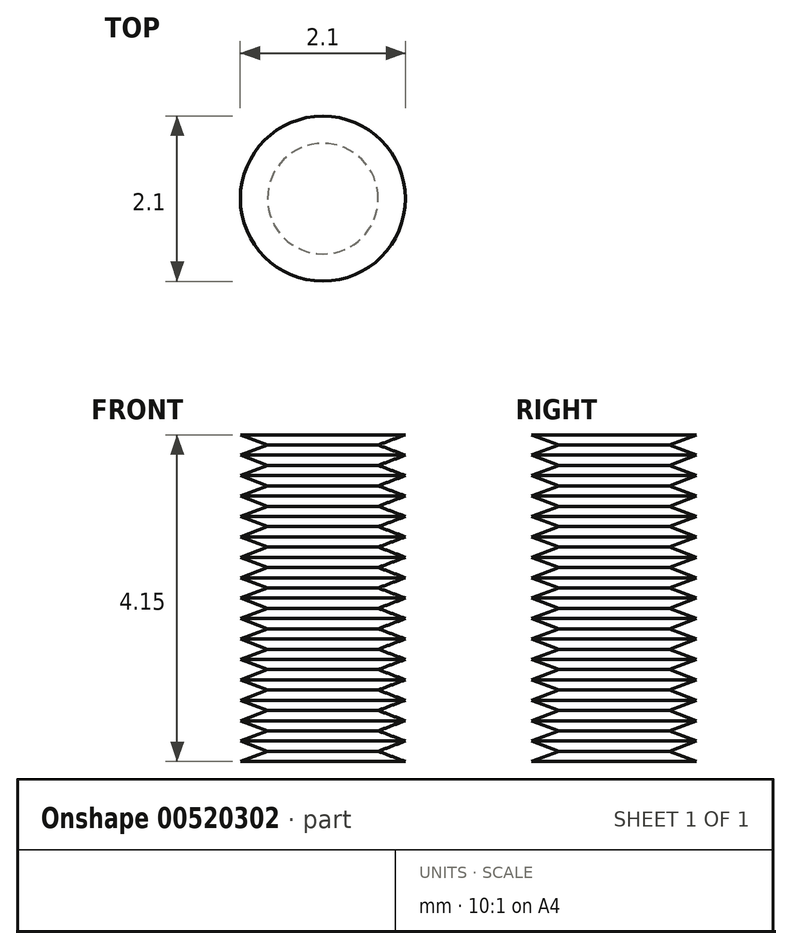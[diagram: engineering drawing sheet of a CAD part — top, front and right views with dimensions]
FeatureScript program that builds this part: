
annotation { "Feature Type Name" : "Feature", "Feature Type Description" : "" }
export const myFeature = defineFeature(function(context is Context, id is Id, definition is map)
    precondition{}
    {
        {
            var Q0;
            Q0=qCreatedBy(makeId("Front.planeOp"),FACE);
            var sketch = newSketch(context, id + "F0", { "sketchPlane" : qUnion([Q0])});
            skLineSegment(sketch, "E0", {"start": v(0, 0) * mm, "end": v(0, 0.01) * mm});
            skLineSegment(sketch, "E1", {"start": v(0, 0.01) * mm, "end": v(-0.07, 0.01) * mm});
            skLineSegment(sketch, "E2", {"start": v(-0.07, 0.01) * mm, "end": v(-0.1, 0) * mm});
            skLineSegment(sketch, "E3", {"start": v(-0.1, 0) * mm, "end": v(0, 0) * mm});
            skLineSegment(sketch, "E4", {"start": v(0, 0.01) * mm, "end": v(0, 0) * mm});
            skSolve(sketch);
        }
        {
            var Q0;
            Q0=makeQuery(id+"F0.imprint","IMPRINT",FACE,{"disambiguationData":[TD([[makeQuery(id+"F0.imprint","IMPRINT",EDGE,{"derivedFrom":sQuery(id+"F0.wireOp",EDGE,"E1")}),1.0]])]});
            var Q1;
            Q1=sQuery(id+"F0.wireOp",EDGE,"E3");
            var Q2;
            Q2=sQuery(id+"F0.wireOp",EDGE,"E2");
            var Q3;
            Q3=sQuery(id+"F0.wireOp",EDGE,"E1");
            var Q4;
            Q4=sQuery(id+"F0.wireOp",EDGE,"E4");
            var Q5;
            Q5=sQuery(id+"F0.wireOp",EDGE,"E0");
            var Q6;
            Q6=sQuery(id+"F0.wireOp",EDGE,"E4");
            revolve(context, id + "F1", {"entities" : qUnion([Q0]), "surfaceEntities" : qUnion([Q1, Q2, Q3, Q4, Q5]), "axis" : qUnion([Q6]), "revolveType" : RevolveType.FULL});
        }
        {
            var Q0;
            Q0=makeQuery(id+"F1.opRevolve","SWEPT_BODY",BODY,{"disambiguationData":[OSD([sQuery(id+"F0.wireOp",EDGE,"E1"),sQuery(id+"F0.wireOp",EDGE,"E2"),sQuery(id+"F0.wireOp",EDGE,"E3"),sQuery(id+"F0.wireOp",EDGE,"E4")])]});
            var Q1;
            Q1=makeQuery(id+"F1.opRevolve","SWEPT_FACE",FACE,{"disambiguationData":[OSD([sQuery(id+"F0.wireOp",EDGE,"E1")])]});
            mirror(context, id + "F2", {"operationType" : NewBodyOperationType.ADD, "entities" : qUnion([Q0]), "mirrorPlane" : qUnion([Q1])});
        }
        {
            var Q0;
            Q0=makeQuery(id+"F1.opRevolve","SWEPT_BODY",BODY,{"disambiguationData":[OSD([sQuery(id+"F0.wireOp",EDGE,"E1"),sQuery(id+"F0.wireOp",EDGE,"E2"),sQuery(id+"F0.wireOp",EDGE,"E3"),sQuery(id+"F0.wireOp",EDGE,"E4")])]});
            var Q1;
            Q1=makeQuery(id+"F2.opPattern","COPY",FACE,{"derivedFrom":makeQuery(id+"F1.opRevolve","SWEPT_FACE",FACE,{"disambiguationData":[OSD([sQuery(id+"F0.wireOp",EDGE,"E3")])]}),"instanceName":"1"});
            mirror(context, id + "F3", {"operationType" : NewBodyOperationType.ADD, "entities" : qUnion([Q0]), "mirrorPlane" : qUnion([Q1])});
        }
        {
            var Q0;
            Q0=makeQuery(id+"F1.opRevolve","SWEPT_BODY",BODY,{"disambiguationData":[OSD([sQuery(id+"F0.wireOp",EDGE,"E1"),sQuery(id+"F0.wireOp",EDGE,"E2"),sQuery(id+"F0.wireOp",EDGE,"E3"),sQuery(id+"F0.wireOp",EDGE,"E4")])]});
            var Q1;
            Q1=makeQuery(id+"F3.opPattern","COPY",FACE,{"derivedFrom":makeQuery(id+"F1.opRevolve","SWEPT_FACE",FACE,{"disambiguationData":[OSD([sQuery(id+"F0.wireOp",EDGE,"E3")])]}),"instanceName":"1"});
            mirror(context, id + "F4", {"operationType" : NewBodyOperationType.ADD, "entities" : qUnion([Q0]), "mirrorPlane" : qUnion([Q1])});
        }
        {
            var Q0;
            Q0=makeQuery(id+"F1.opRevolve","SWEPT_BODY",BODY,{"disambiguationData":[OSD([sQuery(id+"F0.wireOp",EDGE,"E1"),sQuery(id+"F0.wireOp",EDGE,"E2"),sQuery(id+"F0.wireOp",EDGE,"E3"),sQuery(id+"F0.wireOp",EDGE,"E4")])]});
            var Q1;
            Q1=makeQuery(id+"F4.opPattern","COPY",FACE,{"derivedFrom":makeQuery(id+"F1.opRevolve","SWEPT_FACE",FACE,{"disambiguationData":[OSD([sQuery(id+"F0.wireOp",EDGE,"E3")])]}),"instanceName":"1"});
            mirror(context, id + "F5", {"operationType" : NewBodyOperationType.ADD, "entities" : qUnion([Q0]), "mirrorPlane" : qUnion([Q1])});
        }
        {
            var Q0;
            Q0=makeQuery(id+"F1.opRevolve","SWEPT_BODY",BODY,{"disambiguationData":[OSD([sQuery(id+"F0.wireOp",EDGE,"E1"),sQuery(id+"F0.wireOp",EDGE,"E2"),sQuery(id+"F0.wireOp",EDGE,"E3"),sQuery(id+"F0.wireOp",EDGE,"E4")])]});
            var Q1;
            Q1=makeQuery(id+"F5.opPattern","COPY",FACE,{"derivedFrom":makeQuery(id+"F1.opRevolve","SWEPT_FACE",FACE,{"disambiguationData":[OSD([sQuery(id+"F0.wireOp",EDGE,"E3")])]}),"instanceName":"1"});
            mirror(context, id + "F6", {"operationType" : NewBodyOperationType.ADD, "entities" : qUnion([Q0]), "mirrorPlane" : qUnion([Q1])});
        }
        {
            var Q0;
            Q0=makeQuery(id+"F1.opRevolve","SWEPT_BODY",BODY,{"disambiguationData":[OSD([sQuery(id+"F0.wireOp",EDGE,"E1"),sQuery(id+"F0.wireOp",EDGE,"E2"),sQuery(id+"F0.wireOp",EDGE,"E3"),sQuery(id+"F0.wireOp",EDGE,"E4")])]});
            var Q1;
            Q1=qCreatedBy(makeId("Origin.pointOp"),VERTEX);
            transform(context, id + "F7", {"entities" : qUnion([Q0]), "transformType" : TransformType.SCALE_UNIFORMLY, "scale" : 10, "scalePoint" : qUnion([Q1]), "makeCopy" : false});
        }
    });
